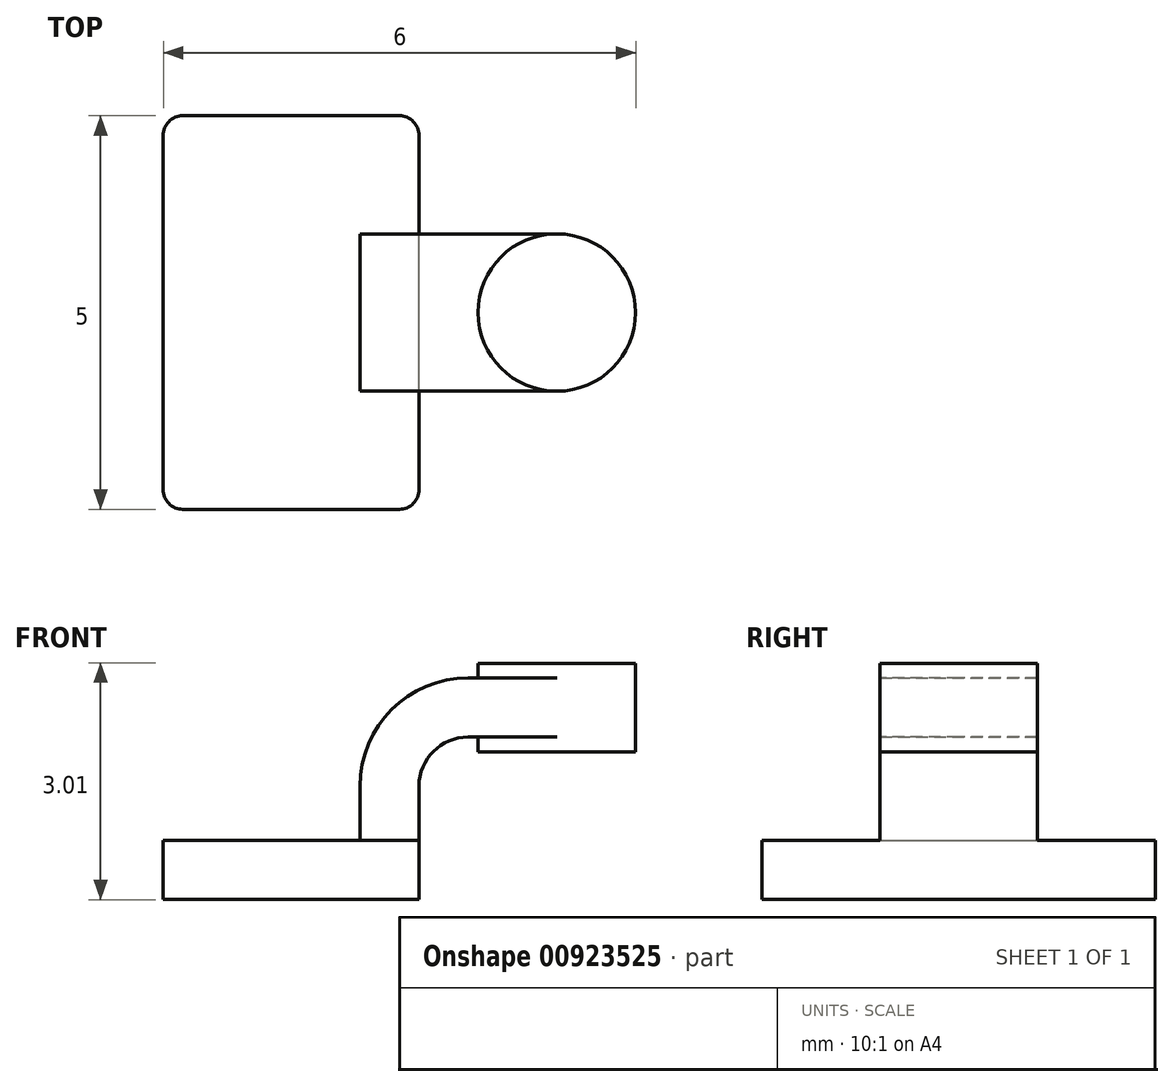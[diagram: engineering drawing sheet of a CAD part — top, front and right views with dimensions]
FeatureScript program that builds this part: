
annotation { "Feature Type Name" : "Feature", "Feature Type Description" : "" }
export const myFeature = defineFeature(function(context is Context, id is Id, definition is map)
    precondition{}
    {
        {
            var Q0;
            Q0=qCreatedBy(makeId("Front.planeOp"),FACE);
            var sketch = newSketch(context, id + "F0", { "sketchPlane" : qUnion([Q0])});
            skLineSegment(sketch, "E0.bottom", {"start": v(-1.63, -0.38) * mm, "end": v(1.63, -0.38) * mm});
            skLineSegment(sketch, "E0.top", {"start": v(-1.63, 0.38) * mm, "end": v(1.63, 0.38) * mm});
            skLineSegment(sketch, "E0.left", {"start": v(-1.63, -0.38) * mm, "end": v(-1.63, 0.38) * mm});
            skLineSegment(sketch, "E0.right", {"start": v(1.63, -0.38) * mm, "end": v(1.63, 0.38) * mm});
            skPoint(sketch, "E0.middle", {"position": v(0, 0) * mm});
            skLineSegment(sketch, "E1.bottom", {"start": v(4.37, 1.5) * mm, "end": v(2.37, 1.5) * mm});
            skLineSegment(sketch, "E1.top", {"start": v(4.37, 2.63) * mm, "end": v(2.37, 2.63) * mm});
            skLineSegment(sketch, "E1.left", {"start": v(4.37, 1.5) * mm, "end": v(4.37, 2.63) * mm});
            skLineSegment(sketch, "E1.right", {"start": v(2.37, 1.5) * mm, "end": v(2.37, 2.63) * mm});
            skPoint(sketch, "E1.middle", {"position": v(3.37, 2.06) * mm});
            skLineSegment(sketch, "E2", {"start": v(1.62, 0.38) * mm, "end": v(1.62, 1.06) * mm});
            skArc(sketch, "E3", {"start": v(1.62, 1.06) * mm, "mid": v(1.8, 1.5) * mm, "end": v(2.25, 1.69) * mm});
            skLineSegment(sketch, "E4", {"start": v(2.25, 1.69) * mm, "end": v(3.37, 1.69) * mm});
            skLineSegment(sketch, "E5.0", {"start": v(2.25, 2.44) * mm, "end": v(3.37, 2.44) * mm});
            skArc(sketch, "E5.1", {"start": v(0.87, 1.06) * mm, "mid": v(1.28, 2.04) * mm, "end": v(2.25, 2.44) * mm});
            skLineSegment(sketch, "E5.2", {"start": v(0.87, 0.38) * mm, "end": v(0.87, 1.06) * mm});
            skFitSpline(sketch, "E6", {"points": [v(-1.63, 0.38) * mm, v(2.25, 2.44) * mm], "startDerivative": vector(-0.02, 3.99) * mm, "endDerivative": vector(4.86, -0.45) * mm});
            skLineSegment(sketch, "E7", {"start": v(3.37, 1.69) * mm, "end": v(3.37, 2.44) * mm});
            skLineSegment(sketch, "E8", {"start": v(3.37, 1.5) * mm, "end": v(3.37, 2.63) * mm});
            skSolve(sketch);
        }
        {
            var Q0;
            Q0=makeQuery(id+"F0.imprint","IMPRINT",FACE,{"disambiguationData":[TD([[makeQuery(id+"F0.imprint","IMPRINT",EDGE,{"derivedFrom":sQuery(id+"F0.wireOp",EDGE,"E0.bottom")}),1.0]])]});
            extrude(context, id + "F1", {"entities" : qUnion([Q0]), "endBound" : BoundingType.SYMMETRIC, "depth" : 5 * mm, "offsetDistance" : 25 * mm});
        }
        {
            var Q0;
            {var subQ1=sQuery(id+"F0.wireOp",EDGE,"E2");Q0=makeQuery(id+"F0.imprint","IMPRINT",FACE,{"disambiguationData":[TD([[makeQuery(id+"F0.imprint","IMPRINT",EDGE,{"derivedFrom":subQ1}),1.0]])]});}
            var Q1;
            {var subQ0=sQuery(id+"F0.wireOp",EDGE,"E4");var subQ1=sQuery(id+"F0.wireOp",EDGE,"E1.right");var subQ2=makeQuery(id+"F0.imprint","INTERSECT",VERTEX,{"derivedFrom":[subQ1,subQ0]});Q1=makeQuery(id+"F0.imprint","IMPRINT",FACE,{"disambiguationData":[TD([[makeQuery(id+"F0.imprint","IMPRINT",EDGE,{"disambiguationData":[TD([[subQ2,-1.0]])],"derivedFrom":subQ1}),-1.0]])]});}
            extrude(context, id + "F2", {"entities" : qUnion([Q0, Q1]), "operationType" : NewBodyOperationType.ADD, "endBound" : BoundingType.SYMMETRIC, "depth" : 2 * mm, "offsetDistance" : 25 * mm});
        }
        {
            var Q0;
            Q0=makeQuery(id+"F0.imprint","IMPRINT",FACE,{"disambiguationData":[TD([[makeQuery(id+"F0.imprint","IMPRINT",EDGE,{"derivedFrom":sQuery(id+"F0.wireOp",EDGE,"E5.1")}),1.0]])]});
            extrude(context, id + "F3", {"entities" : qUnion([Q0]), "operationType" : NewBodyOperationType.ADD, "endBound" : BoundingType.SYMMETRIC, "depth" : .625 * mm, "offsetDistance" : 25 * mm});
        }
        {
            var Q0;
            {var subQ0=sQuery(id+"F0.wireOp",EDGE,"E1.left");Q0=makeQuery(id+"F0.imprint","IMPRINT",FACE,{"disambiguationData":[TD([[makeQuery(id+"F0.imprint","IMPRINT",EDGE,{"derivedFrom":subQ0}),1.0]])]});}
            var Q1;
            Q1=sQuery(id+"F0.wireOp",EDGE,"E8");
            revolve(context, id + "F4", {"operationType" : NewBodyOperationType.ADD, "surfaceOperationType" : NewSurfaceOperationType.NEW, "entities" : qUnion([Q0]), "axis" : qUnion([Q1]), "revolveType" : RevolveType.FULL});
        }
        {
            var Q0;
            Q0=makeQuery(id+"F1.opExtrude","CAP_EDGE",EDGE,{"disambiguationData":[OSD([sQuery(id+"F0.wireOp",EDGE,"E0.right")])],"isStart":false});
            var Q1;
            Q1=makeQuery(id+"F1.opExtrude","CAP_EDGE",EDGE,{"disambiguationData":[OSD([sQuery(id+"F0.wireOp",EDGE,"E0.left")])],"isStart":false});
            var Q2;
            Q2=makeQuery(id+"F1.opExtrude","CAP_EDGE",EDGE,{"disambiguationData":[OSD([sQuery(id+"F0.wireOp",EDGE,"E0.left")])],"isStart":true});
            var Q3;
            Q3=makeQuery(id+"F1.opExtrude","CAP_EDGE",EDGE,{"disambiguationData":[OSD([sQuery(id+"F0.wireOp",EDGE,"E0.right")])],"isStart":true});
            fillet(context, id + "F5", {"entities" : qUnion([Q0, Q1, Q2, Q3]), "radius" : 0.25 * mm, "tangentPropagation" : true, "allowEdgeOverflow" : false});
        }
    });
